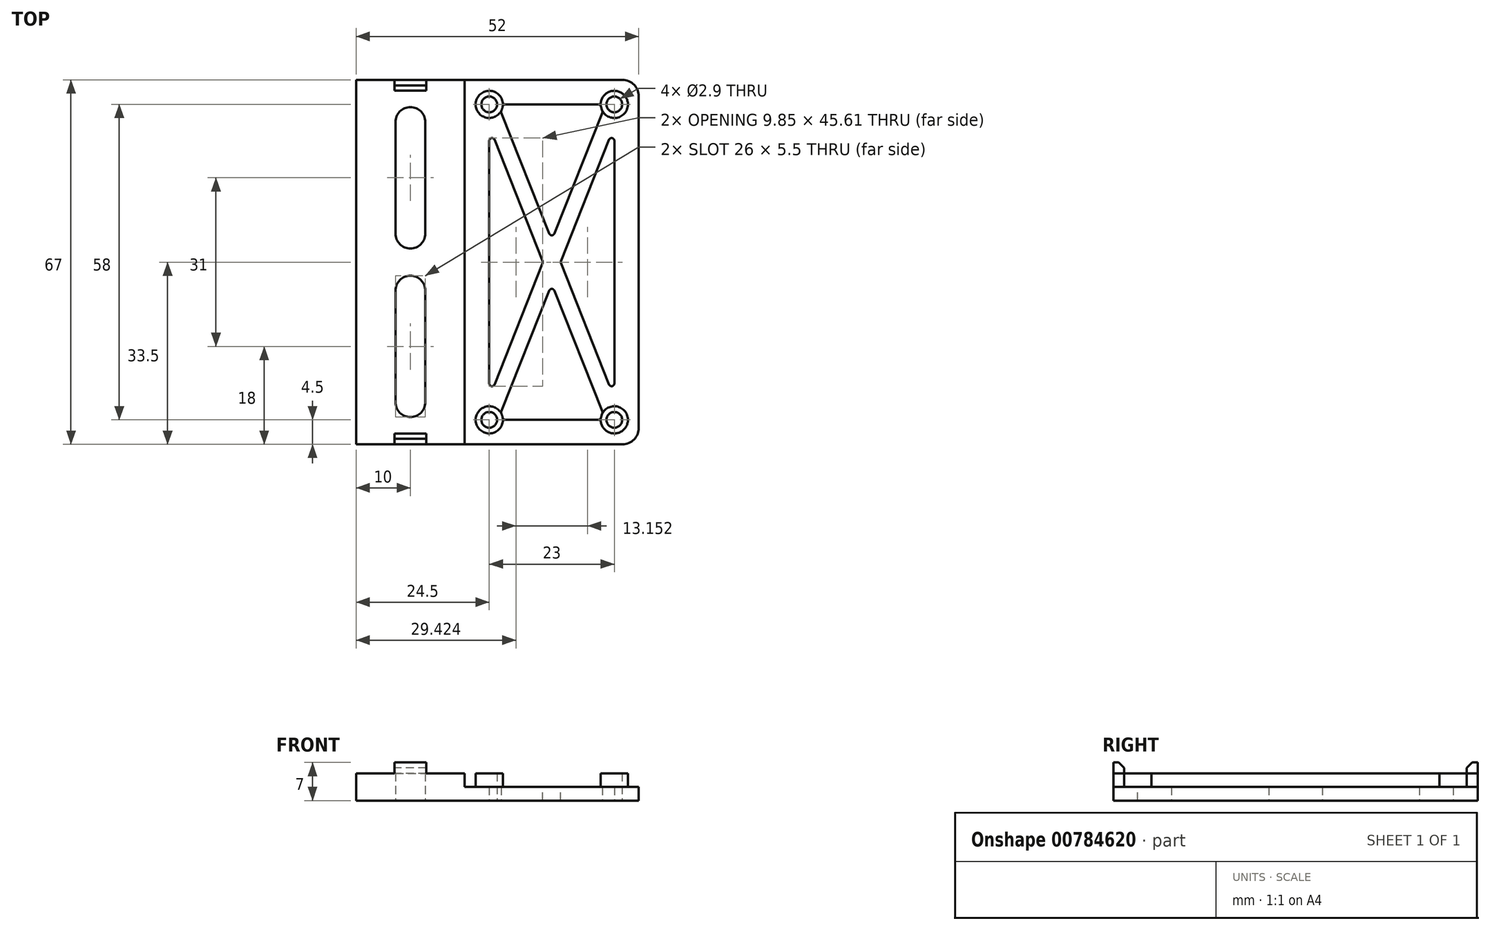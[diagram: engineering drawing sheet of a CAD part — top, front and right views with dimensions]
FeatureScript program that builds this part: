
annotation { "Feature Type Name" : "Feature", "Feature Type Description" : "" }
export const myFeature = defineFeature(function(context is Context, id is Id, definition is map)
    precondition{}
    {
        {
            var Q0;
            Q0=qCreatedBy(makeId("Top.planeOp"),FACE);
            var sketch = newSketch(context, id + "F0", { "sketchPlane" : qUnion([Q0])});
            skLineSegment(sketch, "E0.bottom", {"start": v(11.5, -29) * mm, "end": v(-11.5, -29) * mm, "construction": true});
            skLineSegment(sketch, "E0.top", {"start": v(11.5, 29) * mm, "end": v(-11.5, 29) * mm, "construction": true});
            skLineSegment(sketch, "E0.left", {"start": v(11.5, -29) * mm, "end": v(11.5, 29) * mm, "construction": true});
            skLineSegment(sketch, "E0.right", {"start": v(-11.5, -29) * mm, "end": v(-11.5, 29) * mm, "construction": true});
            skPoint(sketch, "E0.middle", {"position": v(0, 0) * mm});
            skLineSegment(sketch, "E1.bottom", {"start": v(16, -33.5) * mm, "end": v(-16, -33.5) * mm});
            skLineSegment(sketch, "E1.top", {"start": v(16, 33.5) * mm, "end": v(-16, 33.5) * mm});
            skLineSegment(sketch, "E1.left", {"start": v(16, -33.5) * mm, "end": v(16, 33.5) * mm});
            skLineSegment(sketch, "E1.right", {"start": v(-16, -33.5) * mm, "end": v(-16, 33.5) * mm});
            skLineSegment(sketch, "E2", {"start": v(-16, 33.5) * mm, "end": v(-36, 33.5) * mm});
            skLineSegment(sketch, "E3", {"start": v(-36, 33.5) * mm, "end": v(-36, -33.5) * mm});
            skLineSegment(sketch, "E4", {"start": v(-36, -33.5) * mm, "end": v(-16, -33.5) * mm});
            skLineSegment(sketch, "E5.bottom", {"start": v(-23.25, 2.5) * mm, "end": v(-28.75, 2.5) * mm});
            skLineSegment(sketch, "E5.top", {"start": v(-23.25, 28.5) * mm, "end": v(-28.75, 28.5) * mm});
            skLineSegment(sketch, "E5.left", {"start": v(-23.25, 2.5) * mm, "end": v(-23.25, 28.5) * mm});
            skLineSegment(sketch, "E5.right", {"start": v(-28.75, 2.5) * mm, "end": v(-28.75, 28.5) * mm});
            skPoint(sketch, "E5.middle", {"position": v(-26, 15.5) * mm});
            skPoint(sketch, "E5.middle.positionSnap0", {"position": v(-26, 33.5) * mm});
            skPoint(sketch, "E5.centerSnap0", {"position": v(-26, 33.5) * mm});
            skLineSegment(sketch, "E6.bottom", {"start": v(-23.25, -28.5) * mm, "end": v(-28.75, -28.5) * mm});
            skLineSegment(sketch, "E6.top", {"start": v(-23.25, -2.5) * mm, "end": v(-28.75, -2.5) * mm});
            skLineSegment(sketch, "E6.left", {"start": v(-23.25, -28.5) * mm, "end": v(-23.25, -2.5) * mm});
            skLineSegment(sketch, "E6.right", {"start": v(-28.75, -28.5) * mm, "end": v(-28.75, -2.5) * mm});
            skPoint(sketch, "E6.middle", {"position": v(-26, -15.5) * mm});
            skCircle(sketch, "E7", {"center": v(-11.5, 29) * mm, "radius": 1.45 * mm});
            skCircle(sketch, "E8", {"center": v(11.5, 29) * mm, "radius": 1.45 * mm});
            skCircle(sketch, "E9", {"center": v(11.5, -29) * mm, "radius": 1.45 * mm});
            skCircle(sketch, "E10", {"center": v(-11.5, -29) * mm, "radius": 1.45 * mm});
            skCircle(sketch, "E11", {"center": v(-11.5, 29) * mm, "radius": 2.5 * mm});
            skCircle(sketch, "E12", {"center": v(11.5, 29) * mm, "radius": 2.5 * mm});
            skCircle(sketch, "E13", {"center": v(11.5, -29) * mm, "radius": 2.5 * mm});
            skCircle(sketch, "E14", {"center": v(-11.5, -29) * mm, "radius": 2.5 * mm});
            skLineSegment(sketch, "E15.bottom", {"start": v(-23.05, 33.5) * mm, "end": v(-28.95, 33.5) * mm});
            skLineSegment(sketch, "E15.top", {"start": v(-23.05, 31.5) * mm, "end": v(-28.95, 31.5) * mm});
            skLineSegment(sketch, "E15.left", {"start": v(-23.05, 33.5) * mm, "end": v(-23.05, 31.5) * mm});
            skLineSegment(sketch, "E15.right", {"start": v(-28.95, 33.5) * mm, "end": v(-28.95, 31.5) * mm});
            skPoint(sketch, "E15.middle", {"position": v(-26, 32.5) * mm});
            skLineSegment(sketch, "E16.bottom", {"start": v(-23.05, -33.5) * mm, "end": v(-28.95, -33.5) * mm});
            skLineSegment(sketch, "E16.top", {"start": v(-23.05, -31.5) * mm, "end": v(-28.95, -31.5) * mm});
            skLineSegment(sketch, "E16.left", {"start": v(-23.05, -33.5) * mm, "end": v(-23.05, -31.5) * mm});
            skLineSegment(sketch, "E16.right", {"start": v(-28.95, -33.5) * mm, "end": v(-28.95, -31.5) * mm});
            skPoint(sketch, "E16.middle", {"position": v(-26, -32.5) * mm});
            skSolve(sketch);
        }
        {
            var Q0;
            Q0=makeQuery(id+"F0.imprint","IMPRINT",FACE,{"disambiguationData":[TD([[makeQuery(id+"F0.imprint","IMPRINT",EDGE,{"derivedFrom":sQuery(id+"F0.wireOp",EDGE,"E1.right")}),1.0]])]});
            extrude(context, id + "F1", {"entities" : qUnion([Q0]), "depth" : 5 * mm, "offsetDistance" : 25 * mm});
        }
        {
            var Q0;
            Q0=makeQuery(id+"F0.imprint","IMPRINT",FACE,{"disambiguationData":[TD([[makeQuery(id+"F0.imprint","IMPRINT",EDGE,{"derivedFrom":sQuery(id+"F0.wireOp",EDGE,"E1.bottom")}),-1.0]])]});
            var Q1;
            Q1=makeQuery(id+"F0.imprint","IMPRINT",FACE,{"disambiguationData":[TD([[makeQuery(id+"F0.imprint","IMPRINT",EDGE,{"derivedFrom":sQuery(id+"F0.wireOp",EDGE,"E7")}),-1.0]])]});
            var Q2;
            Q2=makeQuery(id+"F0.imprint","IMPRINT",FACE,{"disambiguationData":[TD([[makeQuery(id+"F0.imprint","IMPRINT",EDGE,{"derivedFrom":sQuery(id+"F0.wireOp",EDGE,"E8")}),-1.0]])]});
            var Q3;
            Q3=makeQuery(id+"F0.imprint","IMPRINT",FACE,{"disambiguationData":[TD([[makeQuery(id+"F0.imprint","IMPRINT",EDGE,{"derivedFrom":sQuery(id+"F0.wireOp",EDGE,"E9")}),-1.0]])]});
            var Q4;
            Q4=makeQuery(id+"F0.imprint","IMPRINT",FACE,{"disambiguationData":[TD([[makeQuery(id+"F0.imprint","IMPRINT",EDGE,{"derivedFrom":sQuery(id+"F0.wireOp",EDGE,"E10")}),-1.0]])]});
            extrude(context, id + "F2", {"entities" : qUnion([Q0, Q1, Q2, Q3, Q4]), "operationType" : NewBodyOperationType.ADD, "depth" : 2.5 * mm, "offsetDistance" : 25 * mm});
        }
        {
            var Q0;
            Q0=makeQuery(id+"F0.imprint","IMPRINT",FACE,{"disambiguationData":[TD([[makeQuery(id+"F0.imprint","IMPRINT",EDGE,{"derivedFrom":sQuery(id+"F0.wireOp",EDGE,"E10")}),-1.0]])]});
            var Q1;
            Q1=makeQuery(id+"F0.imprint","IMPRINT",FACE,{"disambiguationData":[TD([[makeQuery(id+"F0.imprint","IMPRINT",EDGE,{"derivedFrom":sQuery(id+"F0.wireOp",EDGE,"E9")}),-1.0]])]});
            var Q2;
            Q2=makeQuery(id+"F0.imprint","IMPRINT",FACE,{"disambiguationData":[TD([[makeQuery(id+"F0.imprint","IMPRINT",EDGE,{"derivedFrom":sQuery(id+"F0.wireOp",EDGE,"E8")}),-1.0]])]});
            var Q3;
            Q3=makeQuery(id+"F0.imprint","IMPRINT",FACE,{"disambiguationData":[TD([[makeQuery(id+"F0.imprint","IMPRINT",EDGE,{"derivedFrom":sQuery(id+"F0.wireOp",EDGE,"E7")}),-1.0]])]});
            var Q4;
            Q4=makeQuery(id+"F2.opExtrude","CAP_FACE",FACE,{"disambiguationData":[OSD([sQuery(id+"F0.wireOp",EDGE,"E1.bottom"),sQuery(id+"F0.wireOp",EDGE,"E1.top"),sQuery(id+"F0.wireOp",EDGE,"E1.left"),sQuery(id+"F0.wireOp",EDGE,"E1.right"),sQuery(id+"F0.wireOp",EDGE,"E7"),sQuery(id+"F0.wireOp",EDGE,"E8"),sQuery(id+"F0.wireOp",EDGE,"E9"),sQuery(id+"F0.wireOp",EDGE,"E10")])],"isStart":false});
            extrude(context, id + "F3", {"entities" : qUnion([Q0, Q1, Q2, Q3]), "operationType" : NewBodyOperationType.ADD, "endBound" : BoundingType.UP_TO_SURFACE, "depth" : 4 * mm, "endBoundEntityFace" : qUnion([Q4]), "hasOffset" : true, "offsetDistance" : 2.5 * mm, "offsetOppositeDirection" : true});
        }
        {
            var Q0;
            Q0=qCreatedBy(makeId("Top.planeOp"),FACE);
            var sketch = newSketch(context, id + "F4", { "sketchPlane" : qUnion([Q0])});
            skCircle(sketch, "E17.0", {"center": v(-11.5, -29) * mm, "radius": 2.5 * mm});
            skCircle(sketch, "E18.0", {"center": v(11.5, -29) * mm, "radius": 2.5 * mm});
            skCircle(sketch, "E19.0", {"center": v(11.5, 29) * mm, "radius": 2.5 * mm});
            skCircle(sketch, "E20.0", {"center": v(-11.5, 29) * mm, "radius": 2.5 * mm});
            skLineSegment(sketch, "E21.0", {"start": v(-11.5, -29) * mm, "end": v(-11.5, 29) * mm});
            skLineSegment(sketch, "E22.0", {"start": v(11.5, -29) * mm, "end": v(-11.5, -29) * mm});
            skLineSegment(sketch, "E23.0", {"start": v(11.5, -29) * mm, "end": v(11.5, 29) * mm});
            skLineSegment(sketch, "E24.0", {"start": v(11.5, 29) * mm, "end": v(-11.5, 29) * mm});
            skLineSegment(sketch, "E25", {"start": v(-11.5, -29) * mm, "end": v(11.5, 29) * mm, "construction": true});
            skLineSegment(sketch, "E26", {"start": v(11.5, -29) * mm, "end": v(-11.5, 29) * mm, "construction": true});
            skArc(sketch, "E27.0.startCap", {"start": v(-10.1, -29.55) * mm, "mid": v(-12.05, -30.4) * mm, "end": v(-12.9, -28.45) * mm});
            skArc(sketch, "E27.0.endCap", {"start": v(10.1, 29.55) * mm, "mid": v(12.05, 30.4) * mm, "end": v(12.9, 28.45) * mm});
            skLineSegment(sketch, "E27.0.left", {"start": v(-12.9, -28.45) * mm, "end": v(10.1, 29.55) * mm});
            skLineSegment(sketch, "E27.0.right", {"start": v(-10.1, -29.55) * mm, "end": v(12.9, 28.45) * mm});
            skArc(sketch, "E27.1.startCap", {"start": v(12.9, -28.45) * mm, "mid": v(12.05, -30.4) * mm, "end": v(10.1, -29.55) * mm});
            skArc(sketch, "E27.1.endCap", {"start": v(-12.9, 28.45) * mm, "mid": v(-12.05, 30.4) * mm, "end": v(-10.1, 29.55) * mm});
            skLineSegment(sketch, "E27.1.left", {"start": v(10.1, -29.55) * mm, "end": v(-12.9, 28.45) * mm});
            skLineSegment(sketch, "E27.1.right", {"start": v(12.9, -28.45) * mm, "end": v(-10.1, 29.55) * mm});
            skSolve(sketch);
        }
        {
            var Q0;
            {var subQ0=sQuery(id+"F4.wireOp",EDGE,"E27.0.left");var subQ1=sQuery(id+"F4.wireOp",EDGE,"E21.0");var subQ2=makeQuery(id+"F4.imprint","INTERSECT",VERTEX,{"derivedFrom":[subQ1,subQ0]});Q0=makeQuery(id+"F4.imprint","IMPRINT",FACE,{"disambiguationData":[TD([[makeQuery(id+"F4.imprint","IMPRINT",EDGE,{"disambiguationData":[TD([[subQ2,-1.0]])],"derivedFrom":subQ1}),-1.0]])]});}
            var Q1;
            {var subQ0=sQuery(id+"F4.wireOp",EDGE,"E27.1.right");var subQ1=sQuery(id+"F4.wireOp",EDGE,"E23.0");var subQ2=makeQuery(id+"F4.imprint","INTERSECT",VERTEX,{"derivedFrom":[subQ1,subQ0]});Q1=makeQuery(id+"F4.imprint","IMPRINT",FACE,{"disambiguationData":[TD([[makeQuery(id+"F4.imprint","IMPRINT",EDGE,{"disambiguationData":[TD([[subQ2,-1.0]])],"derivedFrom":subQ1}),1.0]])]});}
            var Q2;
            {var subQ1=sQuery(id+"F4.wireOp",EDGE,"E17.0");var subQ5=sQuery(id+"F4.wireOp",EDGE,"E22.0");var subQ8=makeQuery(id+"F4.imprint","INTERSECT",VERTEX,{"derivedFrom":[subQ1,subQ5]});Q2=makeQuery(id+"F4.imprint","IMPRINT",FACE,{"disambiguationData":[TD([[makeQuery(id+"F4.imprint","IMPRINT",EDGE,{"disambiguationData":[TD([[subQ8,-1.0]])],"derivedFrom":subQ1}),-1.0]])]});}
            var Q3;
            {var subQ1=sQuery(id+"F4.wireOp",EDGE,"E19.0");var subQ5=sQuery(id+"F4.wireOp",EDGE,"E24.0");var subQ6=makeQuery(id+"F4.imprint","INTERSECT",VERTEX,{"derivedFrom":[subQ1,subQ5]});Q3=makeQuery(id+"F4.imprint","IMPRINT",FACE,{"disambiguationData":[TD([[makeQuery(id+"F4.imprint","IMPRINT",EDGE,{"disambiguationData":[TD([[subQ6,-1.0]])],"derivedFrom":subQ1}),-1.0]])]});}
            extrude(context, id + "F5", {"entities" : qUnion([Q0, Q1, Q2, Q3]), "operationType" : NewBodyOperationType.REMOVE, "depth" : 25 * mm, "offsetDistance" : 25 * mm});
        }
        {
            var Q0;
            Q0=makeQuery(id+"F0.imprint","IMPRINT",FACE,{"disambiguationData":[TD([[makeQuery(id+"F0.imprint","IMPRINT",EDGE,{"derivedFrom":sQuery(id+"F0.wireOp",EDGE,"E16.top")}),1.0]])]});
            var Q1;
            Q1=makeQuery(id+"F0.imprint","IMPRINT",FACE,{"disambiguationData":[TD([[makeQuery(id+"F0.imprint","IMPRINT",EDGE,{"derivedFrom":sQuery(id+"F0.wireOp",EDGE,"E15.top")}),-1.0]])]});
            var Q2;
            Q2=makeQuery(id+"F1.opExtrude","CAP_FACE",FACE,{"disambiguationData":[OSD([sQuery(id+"F0.wireOp",EDGE,"E1.right"),sQuery(id+"F0.wireOp",EDGE,"E2"),sQuery(id+"F0.wireOp",EDGE,"E3"),sQuery(id+"F0.wireOp",EDGE,"E4"),sQuery(id+"F0.wireOp",EDGE,"E5.bottom"),sQuery(id+"F0.wireOp",EDGE,"E5.top"),sQuery(id+"F0.wireOp",EDGE,"E5.left"),sQuery(id+"F0.wireOp",EDGE,"E5.right"),sQuery(id+"F0.wireOp",EDGE,"E6.bottom"),sQuery(id+"F0.wireOp",EDGE,"E6.top"),sQuery(id+"F0.wireOp",EDGE,"E6.left"),sQuery(id+"F0.wireOp",EDGE,"E6.right"),sQuery(id+"F0.wireOp",EDGE,"E15.top"),sQuery(id+"F0.wireOp",EDGE,"E15.left"),sQuery(id+"F0.wireOp",EDGE,"E15.right"),sQuery(id+"F0.wireOp",EDGE,"E16.top"),sQuery(id+"F0.wireOp",EDGE,"E16.left"),sQuery(id+"F0.wireOp",EDGE,"E16.right")])],"isStart":false});
            extrude(context, id + "F6", {"entities" : qUnion([Q0, Q1]), "operationType" : NewBodyOperationType.ADD, "endBound" : BoundingType.UP_TO_SURFACE, "depth" : 25 * mm, "endBoundEntityFace" : qUnion([Q2]), "hasOffset" : true, "offsetDistance" : 2 * mm, "offsetOppositeDirection" : true});
        }
        {
            var Q0;
            Q0=makeQuery(id+"F5.boolean.opBoolean","COPY",EDGE,{"derivedFrom":makeQuery(id+"F5.opExtrude","SWEPT_EDGE",EDGE,{"disambiguationData":[OSD([sQuery(id+"F4.wireOp",EDGE,"E27.0.right"),sQuery(id+"F4.wireOp",EDGE,"E27.1.right")])]})});
            var Q1;
            Q1=makeQuery(id+"F5.boolean.opBoolean","COPY",EDGE,{"derivedFrom":makeQuery(id+"F5.opExtrude","SWEPT_EDGE",EDGE,{"disambiguationData":[OSD([sQuery(id+"F4.wireOp",EDGE,"E27.0.left"),sQuery(id+"F4.wireOp",EDGE,"E27.1.left")])]})});
            var Q2;
            Q2=makeQuery(id+"F5.boolean.opBoolean","COPY",EDGE,{"derivedFrom":makeQuery(id+"F5.opExtrude","SWEPT_EDGE",EDGE,{"disambiguationData":[OSD([sQuery(id+"F4.wireOp",EDGE,"E27.0.right"),sQuery(id+"F4.wireOp",EDGE,"E27.1.left")])]})});
            var Q3;
            Q3=makeQuery(id+"F5.boolean.opBoolean","COPY",EDGE,{"derivedFrom":makeQuery(id+"F5.opExtrude","SWEPT_EDGE",EDGE,{"disambiguationData":[OSD([sQuery(id+"F4.wireOp",EDGE,"E27.0.left"),sQuery(id+"F4.wireOp",EDGE,"E27.1.right")])]})});
            var Q4;
            Q4=makeQuery(id+"F5.boolean.opBoolean","COPY",EDGE,{"derivedFrom":makeQuery(id+"F5.opExtrude","SWEPT_EDGE",EDGE,{"disambiguationData":[OSD([sQuery(id+"F4.wireOp",EDGE,"E21.0"),sQuery(id+"F4.wireOp",EDGE,"E27.1.left")])]})});
            var Q5;
            Q5=makeQuery(id+"F5.boolean.opBoolean","COPY",EDGE,{"derivedFrom":makeQuery(id+"F5.opExtrude","SWEPT_EDGE",EDGE,{"disambiguationData":[OSD([sQuery(id+"F4.wireOp",EDGE,"E21.0"),sQuery(id+"F4.wireOp",EDGE,"E27.0.left")])]})});
            var Q6;
            Q6=makeQuery(id+"F5.boolean.opBoolean","COPY",EDGE,{"derivedFrom":makeQuery(id+"F5.opExtrude","SWEPT_EDGE",EDGE,{"disambiguationData":[OSD([sQuery(id+"F4.wireOp",EDGE,"E17.0"),sQuery(id+"F4.wireOp",EDGE,"E27.0.right")])]})});
            var Q7;
            Q7=makeQuery(id+"F5.boolean.opBoolean","COPY",EDGE,{"derivedFrom":makeQuery(id+"F5.opExtrude","SWEPT_EDGE",EDGE,{"disambiguationData":[OSD([sQuery(id+"F4.wireOp",EDGE,"E17.0"),sQuery(id+"F4.wireOp",EDGE,"E22.0")])]})});
            var Q8;
            Q8=makeQuery(id+"F5.boolean.opBoolean","COPY",EDGE,{"derivedFrom":makeQuery(id+"F5.opExtrude","SWEPT_EDGE",EDGE,{"disambiguationData":[OSD([sQuery(id+"F4.wireOp",EDGE,"E18.0"),sQuery(id+"F4.wireOp",EDGE,"E22.0")])]})});
            var Q9;
            Q9=makeQuery(id+"F5.boolean.opBoolean","COPY",EDGE,{"derivedFrom":makeQuery(id+"F5.opExtrude","SWEPT_EDGE",EDGE,{"disambiguationData":[OSD([sQuery(id+"F4.wireOp",EDGE,"E18.0"),sQuery(id+"F4.wireOp",EDGE,"E27.1.left")])]})});
            var Q10;
            Q10=makeQuery(id+"F5.boolean.opBoolean","COPY",EDGE,{"derivedFrom":makeQuery(id+"F5.opExtrude","SWEPT_EDGE",EDGE,{"disambiguationData":[OSD([sQuery(id+"F4.wireOp",EDGE,"E23.0"),sQuery(id+"F4.wireOp",EDGE,"E27.1.right")])]})});
            var Q11;
            Q11=makeQuery(id+"F5.boolean.opBoolean","COPY",EDGE,{"derivedFrom":makeQuery(id+"F5.opExtrude","SWEPT_EDGE",EDGE,{"disambiguationData":[OSD([sQuery(id+"F4.wireOp",EDGE,"E23.0"),sQuery(id+"F4.wireOp",EDGE,"E27.0.right")])]})});
            var Q12;
            Q12=makeQuery(id+"F5.boolean.opBoolean","COPY",EDGE,{"derivedFrom":makeQuery(id+"F5.opExtrude","SWEPT_EDGE",EDGE,{"disambiguationData":[OSD([sQuery(id+"F4.wireOp",EDGE,"E20.0"),sQuery(id+"F4.wireOp",EDGE,"E27.1.right")])]})});
            var Q13;
            Q13=makeQuery(id+"F5.boolean.opBoolean","COPY",EDGE,{"derivedFrom":makeQuery(id+"F5.opExtrude","SWEPT_EDGE",EDGE,{"disambiguationData":[OSD([sQuery(id+"F4.wireOp",EDGE,"E20.0"),sQuery(id+"F4.wireOp",EDGE,"E24.0")])]})});
            var Q14;
            Q14=makeQuery(id+"F5.boolean.opBoolean","COPY",EDGE,{"derivedFrom":makeQuery(id+"F5.opExtrude","SWEPT_EDGE",EDGE,{"disambiguationData":[OSD([sQuery(id+"F4.wireOp",EDGE,"E19.0"),sQuery(id+"F4.wireOp",EDGE,"E24.0")])]})});
            var Q15;
            Q15=makeQuery(id+"F5.boolean.opBoolean","COPY",EDGE,{"derivedFrom":makeQuery(id+"F5.opExtrude","SWEPT_EDGE",EDGE,{"disambiguationData":[OSD([sQuery(id+"F4.wireOp",EDGE,"E19.0"),sQuery(id+"F4.wireOp",EDGE,"E27.0.left")])]})});
            fillet(context, id + "F7", {"entities" : qUnion([Q0, Q1, Q2, Q3, Q4, Q5, Q6, Q7, Q8, Q9, Q10, Q11, Q12, Q13, Q14, Q15]), "tangentPropagation" : true, "radius" : 0.5 * mm, "defaultsChanged" : true, "vertexSettings" : [], "allowEdgeOverflow" : false});
        }
        {
            var Q0;
            Q0=makeQuery(id+"F2.opExtrude","SWEPT_EDGE",EDGE,{"disambiguationData":[OSD([sQuery(id+"F0.wireOp",EDGE,"E1.bottom"),sQuery(id+"F0.wireOp",EDGE,"E1.left")])]});
            var Q1;
            Q1=makeQuery(id+"F2.opExtrude","SWEPT_EDGE",EDGE,{"disambiguationData":[OSD([sQuery(id+"F0.wireOp",EDGE,"E1.top"),sQuery(id+"F0.wireOp",EDGE,"E1.left")])]});
            fillet(context, id + "F8", {"entities" : qUnion([Q0, Q1]), "tangentPropagation" : true, "radius" : 3 * mm, "defaultsChanged" : true, "vertexSettings" : [], "allowEdgeOverflow" : false});
        }
        {
            var Q0;
            Q0=makeQuery(id+"F1.opExtrude","SWEPT_EDGE",EDGE,{"disambiguationData":[OSD([sQuery(id+"F0.wireOp",EDGE,"E6.top"),sQuery(id+"F0.wireOp",EDGE,"E6.right")])]});
            var Q1;
            Q1=makeQuery(id+"F1.opExtrude","SWEPT_EDGE",EDGE,{"disambiguationData":[OSD([sQuery(id+"F0.wireOp",EDGE,"E6.bottom"),sQuery(id+"F0.wireOp",EDGE,"E6.right")])]});
            var Q2;
            Q2=makeQuery(id+"F1.opExtrude","SWEPT_EDGE",EDGE,{"disambiguationData":[OSD([sQuery(id+"F0.wireOp",EDGE,"E6.bottom"),sQuery(id+"F0.wireOp",EDGE,"E6.left")])]});
            var Q3;
            Q3=makeQuery(id+"F1.opExtrude","SWEPT_EDGE",EDGE,{"disambiguationData":[OSD([sQuery(id+"F0.wireOp",EDGE,"E6.top"),sQuery(id+"F0.wireOp",EDGE,"E6.left")])]});
            var Q4;
            Q4=makeQuery(id+"F1.opExtrude","SWEPT_EDGE",EDGE,{"disambiguationData":[OSD([sQuery(id+"F0.wireOp",EDGE,"E5.top"),sQuery(id+"F0.wireOp",EDGE,"E5.left")])]});
            var Q5;
            Q5=makeQuery(id+"F1.opExtrude","SWEPT_EDGE",EDGE,{"disambiguationData":[OSD([sQuery(id+"F0.wireOp",EDGE,"E5.top"),sQuery(id+"F0.wireOp",EDGE,"E5.right")])]});
            var Q6;
            Q6=makeQuery(id+"F1.opExtrude","SWEPT_EDGE",EDGE,{"disambiguationData":[OSD([sQuery(id+"F0.wireOp",EDGE,"E5.bottom"),sQuery(id+"F0.wireOp",EDGE,"E5.left")])]});
            var Q7;
            Q7=makeQuery(id+"F1.opExtrude","SWEPT_EDGE",EDGE,{"disambiguationData":[OSD([sQuery(id+"F0.wireOp",EDGE,"E5.bottom"),sQuery(id+"F0.wireOp",EDGE,"E5.right")])]});
            fillet(context, id + "F9", {"entities" : qUnion([Q0, Q1, Q2, Q3, Q4, Q5, Q6, Q7]), "tangentPropagation" : true, "radius" : 5.5 / 2 * mm, "defaultsChanged" : true, "vertexSettings" : [], "allowEdgeOverflow" : false});
        }
        {
            var Q0;
            Q0=makeQuery(id+"F6.opExtrude","CAP_EDGE",EDGE,{"disambiguationData":[OSD([sQuery(id+"F0.wireOp",EDGE,"E15.top")])],"isStart":false});
            var Q1;
            Q1=makeQuery(id+"F6.opExtrude","CAP_EDGE",EDGE,{"disambiguationData":[OSD([sQuery(id+"F0.wireOp",EDGE,"E16.top")])],"isStart":false});
            chamfer(context, id + "F10", {"entities" : qUnion([Q0, Q1]), "width" : 1 * mm, "tangentPropagation" : true});
        }
    });
